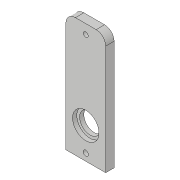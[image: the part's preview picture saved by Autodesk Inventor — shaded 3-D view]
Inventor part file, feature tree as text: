
AUTODESK INVENTOR PART (.ipt)
format: ipt  version: 2018.3 (Build 223284000, 284)  size: 190,976 bytes
history: native  units: in
note: dims shown in document units (in); Inventor stores cm internally (conversion verified against a paired STEP export)
features: extrude x4, sketch x4, fillet x1
ambient origin geometry x8: Origin, YZ Plane, XZ Plane, XY Plane, X Axis, Y Axis, Z Axis, Center Point
bodies: Solid1 (feature_tree)
feature tree (9):
  extrude  "Extrusion1"  Depth=0.221in TaperAngle=0.0deg
  extrude  "Extrusion2"  Depth=0.221in TaperAngle=0.0deg
  extrude  "Extrusion3"  Depth=0.221in
  fillet  "Fillet1"  Radius=0.221in
  extrude  "Extrusion5"  Depth=1.0429in
  sketch  "Sketch1"  dims[d0=0.6925in d3=1.0429in d4=0.5215in d5=2.3125in d6=3.125in d8=0.221in d9=0.0in]
  sketch  "Sketch2"  dims[d10=0.126in d12=0.25in d13=0.221in d14=0.0in]
  sketch  "Sketch3"  dims[d15=0.125in d17=0.136in d18=0.628in d19=0.221in d20=0.0in]
  sketch  "Sketch5"  dims[d21=0.25in d25=1.0429in d26=0.5215in d27=0.5215in d28=0.545in d29=0.1105in d30=0.0in]
